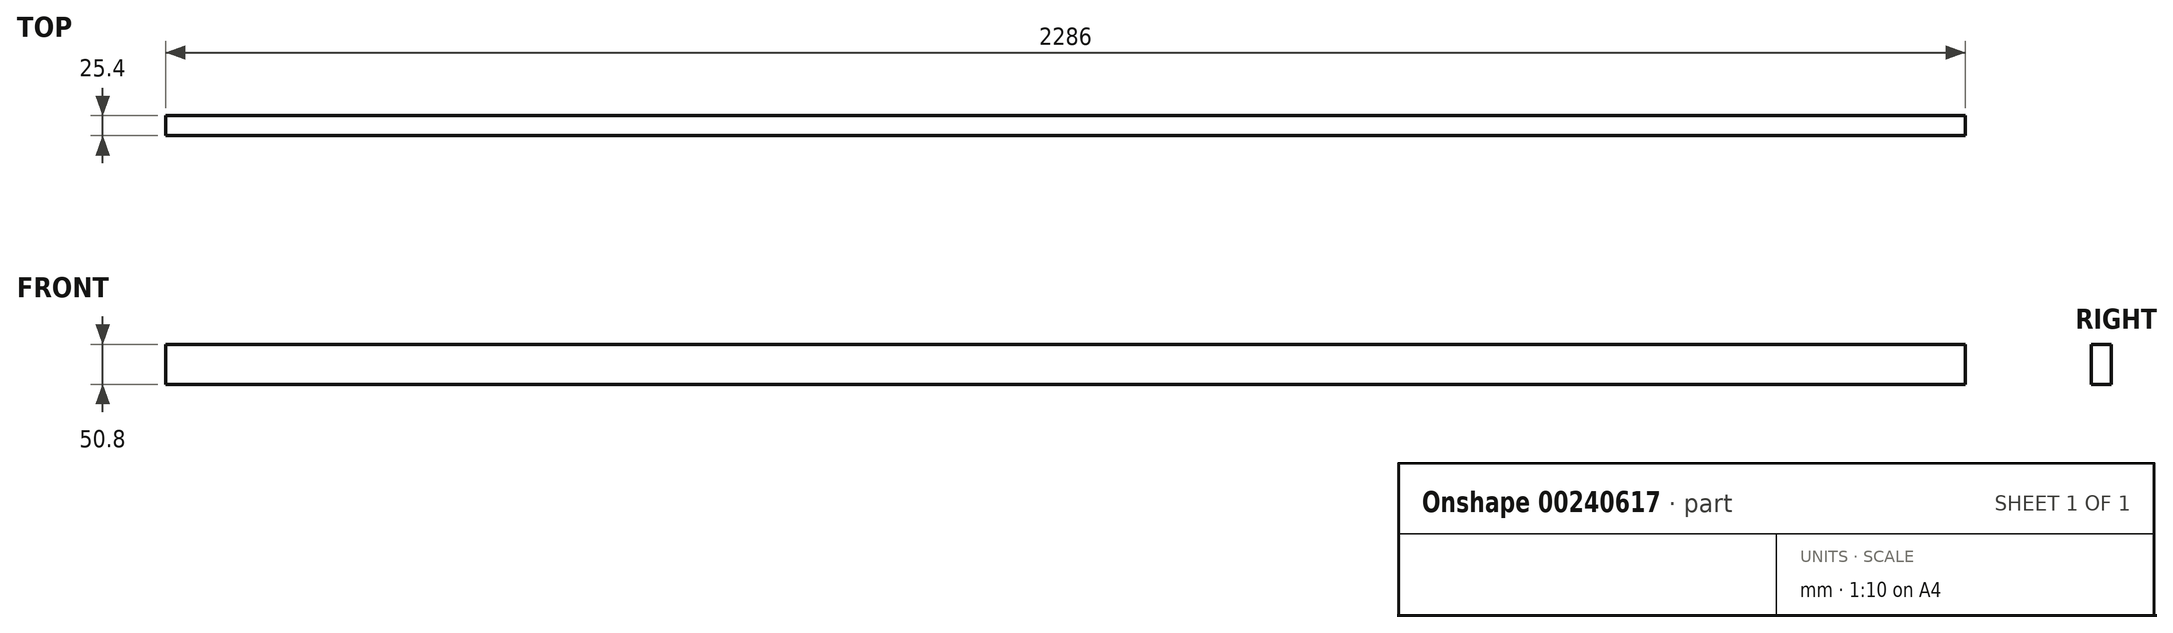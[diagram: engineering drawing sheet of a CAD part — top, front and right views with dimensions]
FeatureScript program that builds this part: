
annotation { "Feature Type Name" : "Feature", "Feature Type Description" : "" }
export const myFeature = defineFeature(function(context is Context, id is Id, definition is map)
    precondition{}
    {
        {
            var Q0;
            Q0=qCreatedBy(makeId("Right.planeOp"),FACE);
            var sketch = newSketch(context, id + "F0", { "sketchPlane" : qUnion([Q0])});
            skLineSegment(sketch, "E0.bottom", {"start": v(-12.7, 25.4) * mm, "end": v(12.7, 25.4) * mm});
            skLineSegment(sketch, "E0.top", {"start": v(-12.7, -25.4) * mm, "end": v(12.7, -25.4) * mm});
            skLineSegment(sketch, "E0.left", {"start": v(-12.7, 25.4) * mm, "end": v(-12.7, -25.4) * mm});
            skLineSegment(sketch, "E0.right", {"start": v(12.7, 25.4) * mm, "end": v(12.7, -25.4) * mm});
            skSolve(sketch);
        }
        {
            var Q0;
            Q0=makeQuery(id+"F0.imprint","IMPRINT",FACE,{"disambiguationData":[TD([[makeQuery(id+"F0.imprint","IMPRINT",EDGE,{"derivedFrom":sQuery(id+"F0.wireOp",EDGE,"E0.bottom")}),-1.0]])]});
            extrude(context, id + "F1", {"entities" : qUnion([Q0]), "endBound" : BoundingType.SYMMETRIC, "depth" : 2286 * mm, "offsetDistance" : 25.4 * mm});
        }
    });
